FCSTD DOCUMENT  (FreeCAD 0.18R)
Label: grip
License: All rights reserved
LicenseURL: http://en.wikipedia.org/wiki/All_rights_reserved
objects: App::Part×3, Sketcher::SketchObject×3
note: 3 computed .brp shape members not serialized (recipe doc carries the construction recipe); baked Part::Feature solids carry a one-line shape summary decoded from their .brp

FEATURE [App::Part] Part  label="electabuzz_grip_handle"
  Origin = -> Origin
FEATURE [Sketcher::SketchObject] Sketch  label="main"
  MapMode = 2
  Support = -> [Part]
  sketch-geometry (4):
    g0: LineSegment StartX=-40 StartY=-60 StartZ=0 EndX=40 EndY=-60 EndZ=0
    g1: LineSegment StartX=-30 StartY=60 StartZ=0 EndX=30 EndY=60 EndZ=0
    g2: ArcOfCircle CenterX=-215 CenterY=15 CenterZ=0 NormalX=0 NormalY=0 NormalZ=1 AngleXU=0 Radius=190.394 StartAngle=5.87829 EndAngle=6.52179
    g3: ArcOfCircle CenterX=215 CenterY=15 CenterZ=0 NormalX=0 NormalY=0 NormalZ=1 AngleXU=0 Radius=190.394 StartAngle=2.90298 EndAngle=3.54648
  constraints (14):
    c: Parallel(g1,g0)
    c: DistanceX(g0,g-1) = 40
    c: DistanceX(g-1,g0) = 40
    c: Parallel(g-1,g0)
    c: DistanceY(g0,g-1) = 60
    c: DistanceY(g-1,g1) = 60
    c: Coincident(g3,g1)
    c: Coincident(g3,g0)
    c: Coincident(g2,g0)
    c: Coincident(g2,g1)
    c: DistanceX(g1,g1) = 60
    c: DistanceX(g-1,g1) = 30
    c: DistanceY(g-1,g2) = 15
    c: DistanceY(g3,g2) = 0
FEATURE [Sketcher::SketchObject] Sketch001  label="cables-back"
  Placement = pos=(0,0,0) rot=(1,0,0;1.5708rad)
  sketch-geometry (3):
    g0: Circle CenterX=-5 CenterY=0 CenterZ=0 NormalX=0 NormalY=0 NormalZ=1 AngleXU=0 Radius=5
    g1: Circle CenterX=5 CenterY=0 CenterZ=0 NormalX=0 NormalY=0 NormalZ=1 AngleXU=0 Radius=5
    g2: Circle CenterX=0 CenterY=2.5 CenterZ=0 NormalX=0 NormalY=0 NormalZ=1 AngleXU=0 Radius=2.5
  constraints (9):
    c: Radius(g1) = 5
    c: Radius(g0) = 5
    c: DistanceY(g1,g0) = 0
    c: DistanceY(g1,g-1) = 0
    c: DistanceX(g0,g1) = 10
    c: DistanceX(g0,g-1) = 5
    c: DistanceX(g-1,g2) = 0
    c: Radius(g2) = 2.5
    c: DistanceY(g-1,g2) = 2.5
FEATURE [App::Part] Part001  label="electabuzz_grip_contacts"
  Origin = -> Origin001
FEATURE [Sketcher::SketchObject] Sketch002
  MapMode = 2
  Support = -> [Sketch]
FEATURE [App::Part] Part002  label="electabuzz_grip_connector"
  Origin = -> Origin002
